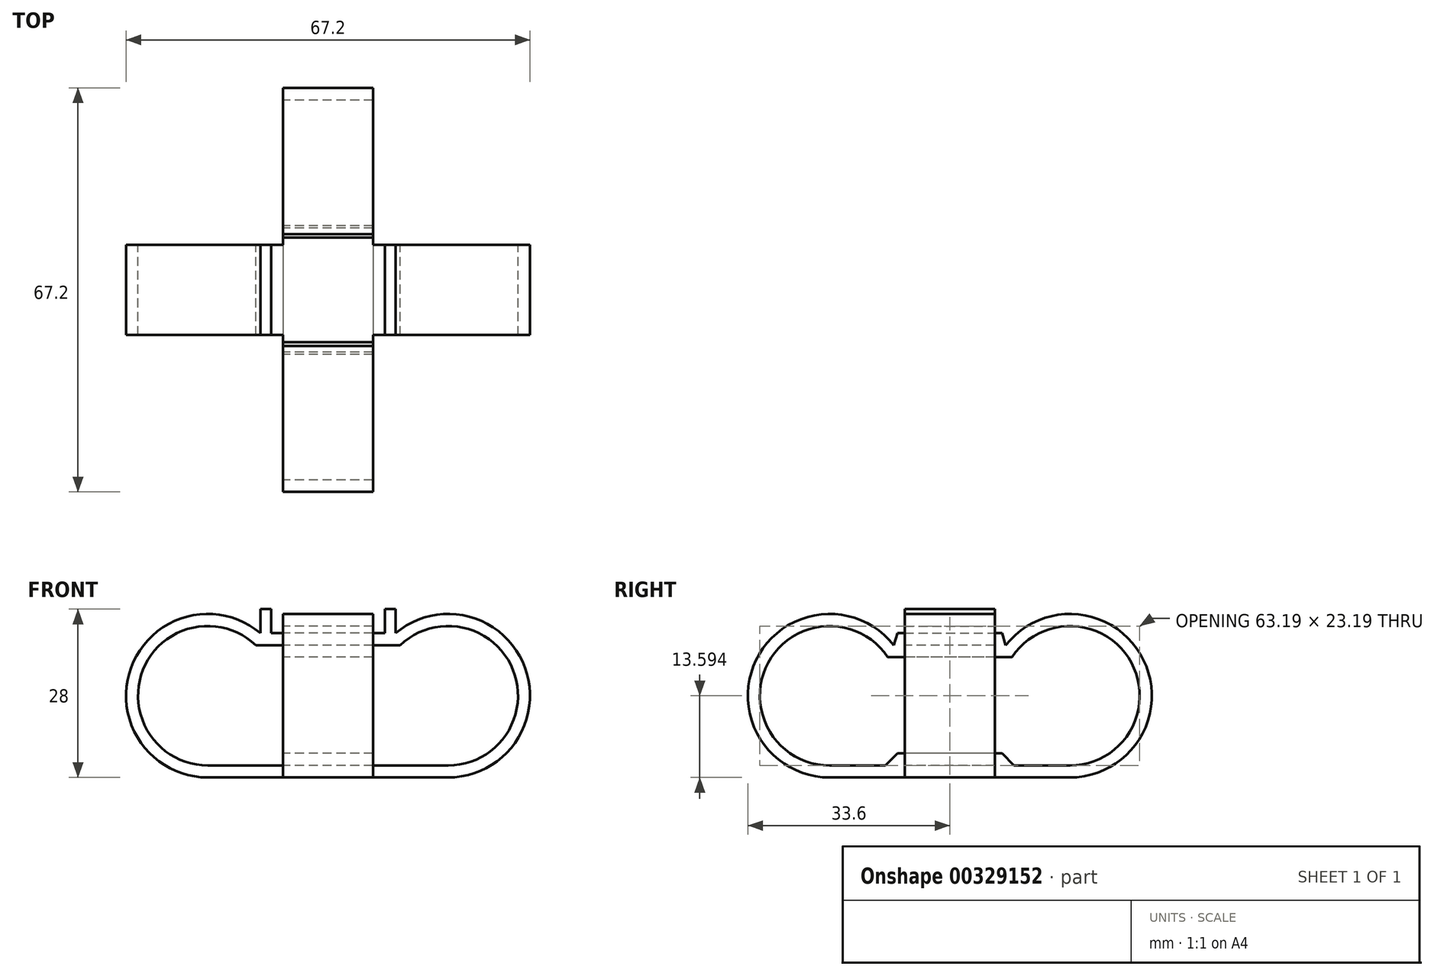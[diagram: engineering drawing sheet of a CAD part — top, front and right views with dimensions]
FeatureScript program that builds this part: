
annotation { "Feature Type Name" : "Feature", "Feature Type Description" : "" }
export const myFeature = defineFeature(function(context is Context, id is Id, definition is map)
    precondition{}
    {
        {
            var Q0;
            Q0=qCreatedBy(makeId("Front.planeOp"),FACE);
            var sketch = newSketch(context, id + "F0", { "sketchPlane" : qUnion([Q0])});
            skLineSegment(sketch, "E0.bottom", {"start": v(12, 10) * mm, "end": v(-12, 10) * mm});
            skLineSegment(sketch, "E0.top", {"start": v(20, -10) * mm, "end": v(-20, -10) * mm});
            skPoint(sketch, "E0.middle", {"position": v(0, 0) * mm});
            skArc(sketch, "E1", {"start": v(-20, -10) * mm, "mid": v(-30.77, 5.9) * mm, "end": v(-12, 10) * mm});
            skPoint(sketch, "E2.orphan", {"position": v(-20, 10) * mm});
            skArc(sketch, "E3.MirrorCS", {"start": v(20, -10) * mm, "mid": v(30.77, 5.9) * mm, "end": v(12, 10) * mm});
            skPoint(sketch, "E4.orphan", {"position": v(20, 10) * mm});
            skLineSegment(sketch, "E5.0", {"start": v(9.44, 12) * mm, "end": v(-9.44, 12) * mm});
            skArc(sketch, "E5.1", {"start": v(20, -12) * mm, "mid": v(32.77, 6.26) * mm, "end": v(11.24, 12) * mm});
            skLineSegment(sketch, "E5.2", {"start": v(20, -12) * mm, "end": v(-20, -12) * mm});
            skArc(sketch, "E5.3", {"start": v(-20, -12) * mm, "mid": v(-32.77, 6.26) * mm, "end": v(-11.24, 12) * mm});
            skLineSegment(sketch, "E6", {"start": v(-11.24, 12) * mm, "end": v(-11.24, 16) * mm});
            skLineSegment(sketch, "E7", {"start": v(-11.24, 16) * mm, "end": v(-9.44, 16) * mm});
            skLineSegment(sketch, "E8", {"start": v(-9.44, 16) * mm, "end": v(-9.44, 12) * mm});
            skLineSegment(sketch, "E9.MirrorCS", {"start": v(9.44, 16) * mm, "end": v(9.44, 12) * mm});
            skLineSegment(sketch, "E10.MirrorCS", {"start": v(11.24, 16) * mm, "end": v(9.44, 16) * mm});
            skLineSegment(sketch, "E11.MirrorCS", {"start": v(11.24, 12) * mm, "end": v(11.24, 16) * mm});
            skSolve(sketch);
        }
        {
            var Q0;
            Q0 = qSketchRegion(id + "F0", true);
            extrude(context, id + "F1", {"entities" : qUnion([Q0]), "endBound" : BoundingType.SYMMETRIC, "depth" : 15 * mm});
        }
        {
            var Q0;
            Q0=qCreatedBy(makeId("Right.planeOp"),FACE);
            var sketch = newSketch(context, id + "F2", { "sketchPlane" : qUnion([Q0])});
            skLineSegment(sketch, "E12.top", {"start": v(7.5, -10) * mm, "end": v(-7.5, -10) * mm});
            skPoint(sketch, "E12.middle", {"position": v(0, 0) * mm});
            skArc(sketch, "E13", {"start": v(-20, -10) * mm, "mid": v(-30.22, 7.1) * mm, "end": v(-10.33, 8) * mm});
            skLineSegment(sketch, "E14.2", {"start": v(20, -12) * mm, "end": v(7.5, -12) * mm});
            skArc(sketch, "E14.3", {"start": v(-20, -12) * mm, "mid": v(-32.23, 7.55) * mm, "end": v(-9.3, 10) * mm});
            skLineSegment(sketch, "E15.0", {"start": v(10.33, 8) * mm, "end": v(-10.33, 8) * mm});
            skLineSegment(sketch, "E16.0", {"start": v(8.7, -8) * mm, "end": v(-8.7, -8) * mm});
            skPoint(sketch, "E17.orphan", {"position": v(-12, 10) * mm});
            skPoint(sketch, "E18.start.orphan", {"position": v(-20, 15.2) * mm});
            skLineSegment(sketch, "E19", {"start": v(-9.3, 10) * mm, "end": v(-8.7, 12) * mm});
            skLineSegment(sketch, "E20.0", {"start": v(-7.5, -12) * mm, "end": v(-7.5, 15.2) * mm, "construction": true});
            skLineSegment(sketch, "E20.1", {"start": v(7.5, -12) * mm, "end": v(7.5, 15.2) * mm, "construction": true});
            skLineSegment(sketch, "E21", {"start": v(-8.7, 12) * mm, "end": v(-7.5, 12) * mm});
            skLineSegment(sketch, "E22", {"start": v(-7.5, 12) * mm, "end": v(-7.5, 10) * mm});
            skLineSegment(sketch, "E23", {"start": v(-7.5, -12) * mm, "end": v(-20, -12) * mm});
            skLineSegment(sketch, "E24", {"start": v(7.5, -12) * mm, "end": v(-7.5, -12) * mm, "construction": true});
            skLineSegment(sketch, "E25", {"start": v(-8.7, -8) * mm, "end": v(-10.7, -10) * mm});
            skLineSegment(sketch, "E26", {"start": v(-10.7, -10) * mm, "end": v(-20, -10) * mm});
            skLineSegment(sketch, "E27.trimOffspring", {"start": v(-7.5, 12) * mm, "end": v(-8.7, 12) * mm});
            skLineSegment(sketch, "E28.MirrorCS", {"start": v(8.7, 12) * mm, "end": v(7.5, 12) * mm});
            skLineSegment(sketch, "E29.MirrorCS", {"start": v(7.5, 12) * mm, "end": v(8.7, 12) * mm});
            skLineSegment(sketch, "E30.MirrorCS", {"start": v(7.5, 12) * mm, "end": v(7.5, 10) * mm});
            skLineSegment(sketch, "E31.MirrorCS", {"start": v(8.7, -8) * mm, "end": v(10.7, -10) * mm});
            skLineSegment(sketch, "E32.MirrorCS", {"start": v(10.7, -10) * mm, "end": v(20, -10) * mm});
            skLineSegment(sketch, "E33.MirrorCS", {"start": v(9.3, 10) * mm, "end": v(8.7, 12) * mm});
            skPoint(sketch, "E34.MirrorP", {"position": v(20, 15.2) * mm});
            skArc(sketch, "E35.MirrorCS", {"start": v(20, -12) * mm, "mid": v(32.23, 7.55) * mm, "end": v(9.3, 10) * mm});
            skArc(sketch, "E36.MirrorCS", {"start": v(20, -10) * mm, "mid": v(30.22, 7.1) * mm, "end": v(10.33, 8) * mm});
            skLineSegment(sketch, "E37.MirrorCS", {"start": v(7.5, -12) * mm, "end": v(20, -12) * mm});
            skLineSegment(sketch, "E38.trimOffspring", {"start": v(7.5, 10) * mm, "end": v(-7.5, 10) * mm});
            skPoint(sketch, "E12.bottom.start.orphan", {"position": v(12, 10) * mm});
            skLineSegment(sketch, "E39", {"start": v(7.5, -12) * mm, "end": v(7.5, -10) * mm});
            skLineSegment(sketch, "E40", {"start": v(-7.5, -12) * mm, "end": v(-7.5, -10) * mm});
            skSolve(sketch);
        }
        {
            var Q0;
            Q0 = qSketchRegion(id + "F2", true);
            extrude(context, id + "F3", {"entities" : qUnion([Q0]), "operationType" : NewBodyOperationType.ADD, "endBound" : BoundingType.SYMMETRIC, "depth" : 15 * mm});
        }
    });
